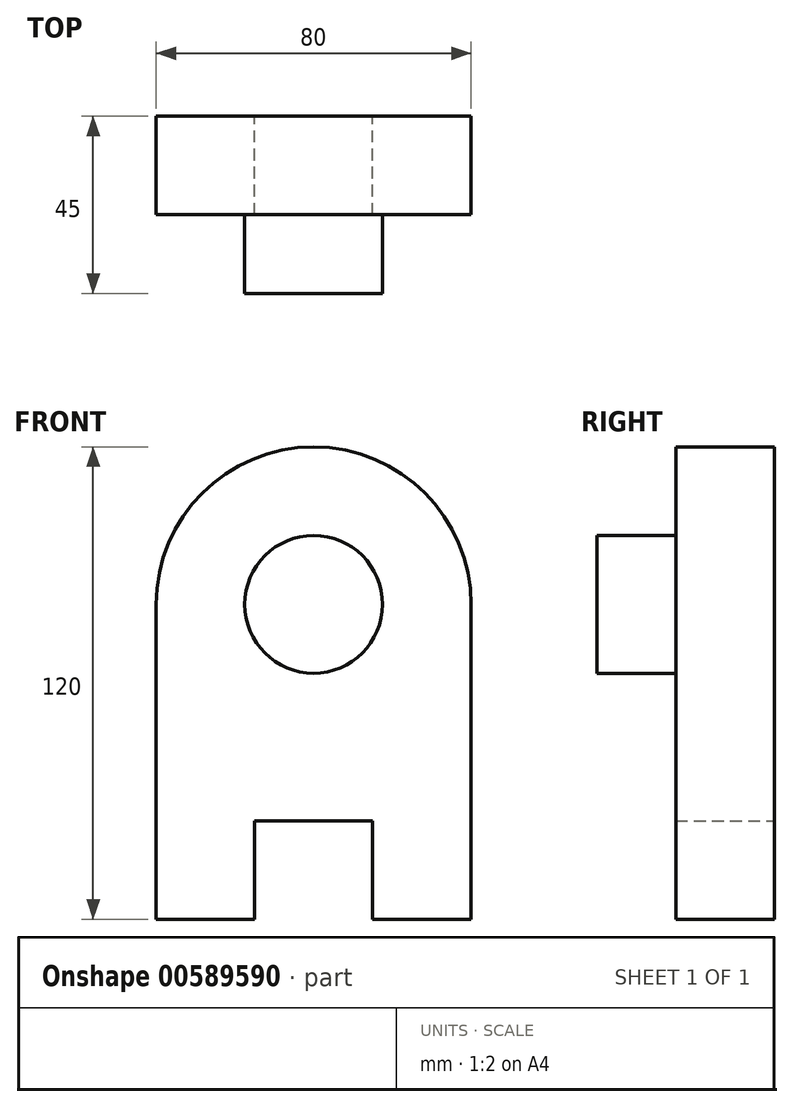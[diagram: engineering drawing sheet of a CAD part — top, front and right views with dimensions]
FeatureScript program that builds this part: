
annotation { "Feature Type Name" : "Feature", "Feature Type Description" : "" }
export const myFeature = defineFeature(function(context is Context, id is Id, definition is map)
    precondition{}
    {
        {
            var Q0;
            Q0=qCreatedBy(makeId("Front.planeOp"),FACE);
            var sketch = newSketch(context, id + "F0", { "sketchPlane" : qUnion([Q0])});
            skLineSegment(sketch, "E0.bottom", {"start": v(0, 80) * mm, "end": v(22.5, 80) * mm});
            skLineSegment(sketch, "E0.top", {"start": v(0, 0) * mm, "end": v(25, 0) * mm});
            skLineSegment(sketch, "E0.left", {"start": v(0, 80) * mm, "end": v(0, 0) * mm});
            skLineSegment(sketch, "E0.right", {"start": v(80, 80) * mm, "end": v(80, 0) * mm});
            skLineSegment(sketch, "E1", {"start": v(25, 0) * mm, "end": v(25, 25) * mm});
            skLineSegment(sketch, "E2", {"start": v(55, 25) * mm, "end": v(25, 25) * mm});
            skLineSegment(sketch, "E3", {"start": v(55, 25) * mm, "end": v(55, 0) * mm});
            skPoint(sketch, "E4.start.orphan", {"position": v(0, -5.02) * mm});
            skLineSegment(sketch, "E5.trimOffspring", {"start": v(55, 0) * mm, "end": v(80, 0) * mm});
            skCircle(sketch, "E6", {"center": v(40, 80) * mm, "radius": 17.5 * mm});
            skPoint(sketch, "E7.orphan", {"position": v(0, 80) * mm});
            skArc(sketch, "E8", {"start": v(80, 80) * mm, "mid": v(40, 120) * mm, "end": v(0, 80) * mm});
            skLineSegment(sketch, "E9.trimOffspring", {"start": v(57.5, 80) * mm, "end": v(80, 80) * mm});
            skSolve(sketch);
        }
        {
            var Q0;
            Q0 = qSketchRegion(id + "F0", true);
            extrude(context, id + "F1", {"entities" : qUnion([Q0]), "depth" : 25 * mm, "offsetDistance" : 25 * mm});
        }
        {
            var Q0;
            {var subQ0=sQuery(id+"F0.wireOp",EDGE,"E6");var subQ1=makeQuery(id+"F0.imprint","INTERSECT",VERTEX,{"derivedFrom":[sQuery(id+"F0.wireOp",EDGE,"E0.bottom"),subQ0]});Q0=makeQuery(id+"F0.imprint","IMPRINT",FACE,{"disambiguationData":[TD([[makeQuery(id+"F0.imprint","IMPRINT",EDGE,{"disambiguationData":[TD([[subQ1,1.0]])],"derivedFrom":subQ0}),1.0]])]});}
            extrude(context, id + "F2", {"entities" : qUnion([Q0]), "operationType" : NewBodyOperationType.ADD, "depth" : 45 * mm, "offsetDistance" : 25 * mm});
        }
    });
